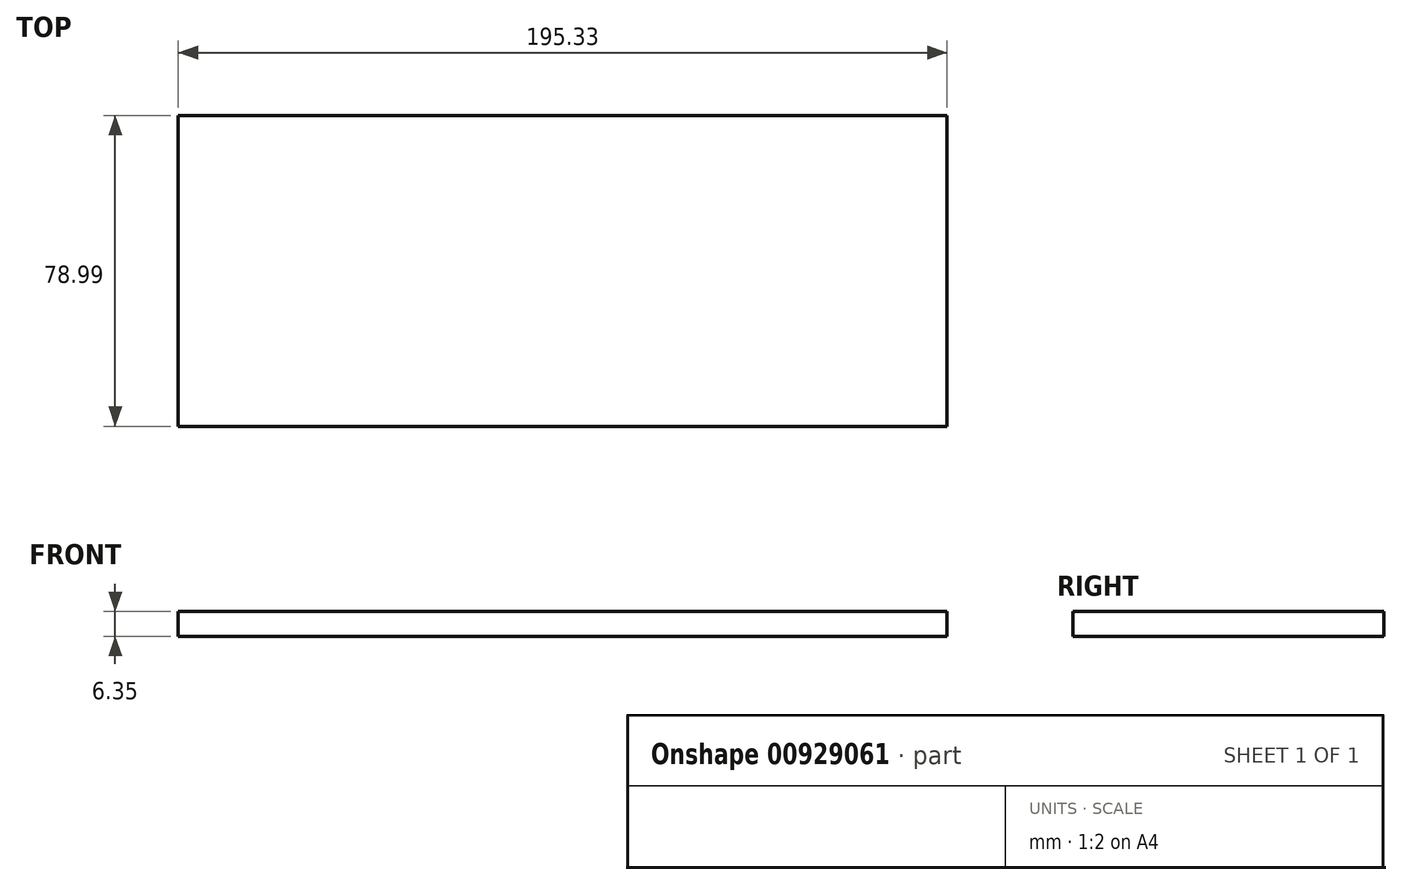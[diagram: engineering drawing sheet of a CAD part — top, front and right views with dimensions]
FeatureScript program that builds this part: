
annotation { "Feature Type Name" : "Feature", "Feature Type Description" : "" }
export const myFeature = defineFeature(function(context is Context, id is Id, definition is map)
    precondition{}
    {
        {
            var Q0;
            Q0=qCreatedBy(makeId("Top.planeOp"),FACE);
            var sketch = newSketch(context, id + "F0", { "sketchPlane" : qUnion([Q0])});
            skLineSegment(sketch, "E0.bottom", {"start": v(0, 0) * mm, "end": v(195.33, 0) * mm});
            skLineSegment(sketch, "E0.top", {"start": v(0, -79) * mm, "end": v(195.33, -79) * mm});
            skLineSegment(sketch, "E0.left", {"start": v(0, 0) * mm, "end": v(0, -79) * mm});
            skLineSegment(sketch, "E0.right", {"start": v(195.33, 0) * mm, "end": v(195.33, -79) * mm});
            skSolve(sketch);
        }
        {
            var Q0;
            Q0=makeQuery(id+"F0.imprint","IMPRINT",FACE,{"disambiguationData":[TD([[makeQuery(id+"F0.imprint","IMPRINT",EDGE,{"derivedFrom":sQuery(id+"F0.wireOp",EDGE,"E0.bottom")}),-1.0]])]});
            extrude(context, id + "F1", {"entities" : qUnion([Q0]), "depth" : 6.35 * mm, "offsetDistance" : 25.4 * mm});
        }
    });
